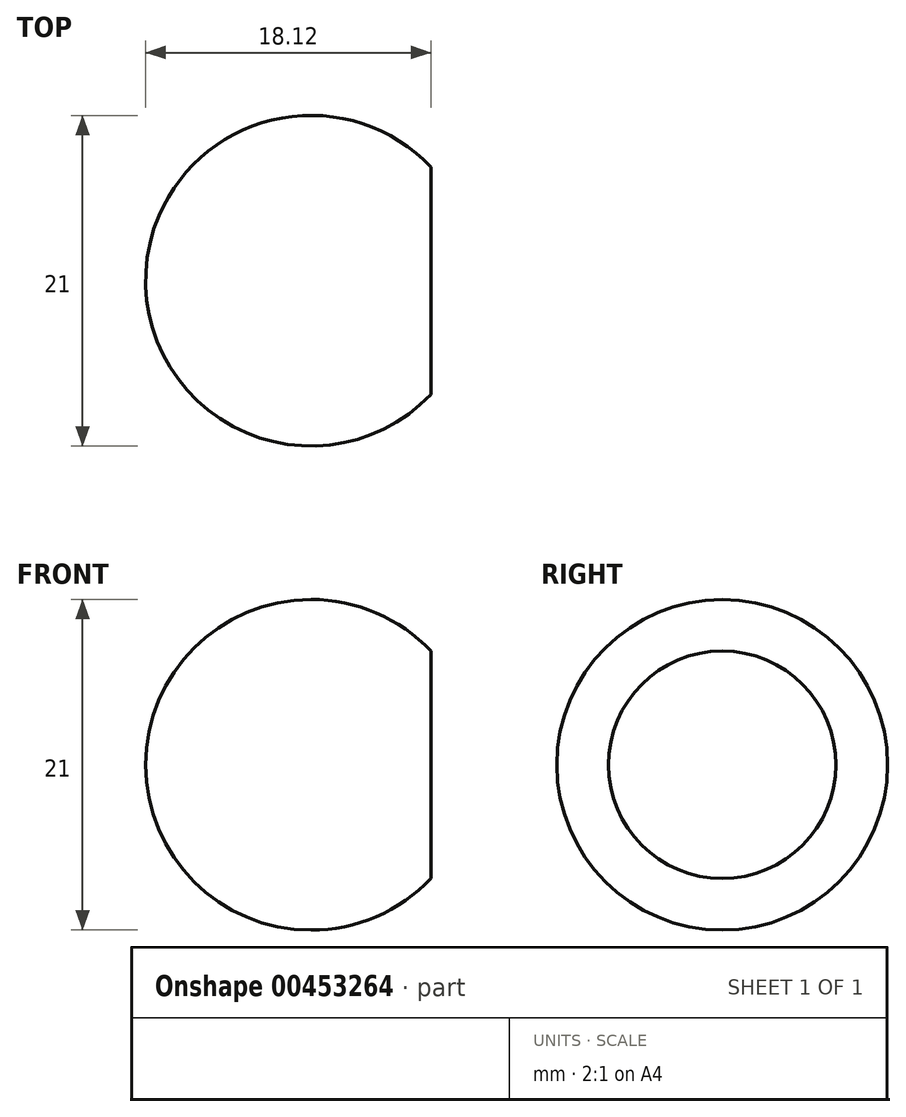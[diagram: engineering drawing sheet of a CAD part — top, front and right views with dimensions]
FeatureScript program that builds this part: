
annotation { "Feature Type Name" : "Feature", "Feature Type Description" : "" }
export const myFeature = defineFeature(function(context is Context, id is Id, definition is map)
    precondition{}
    {
        {
            var Q0;
            Q0=qCreatedBy(makeId("Right.planeOp"),FACE);
            var sketch = newSketch(context, id + "F0", { "sketchPlane" : qUnion([Q0])});
            skCircle(sketch, "E0", {"center": v(0, 0) * mm, "radius": 10.5 * mm});
            skLineSegment(sketch, "E1", {"start": v(0, 10.5) * mm, "end": v(0, -10.5) * mm});
            skSolve(sketch);
        }
        {
            var Q0;
            {var subQ0=sQuery(id+"F0.wireOp",EDGE,"E1");Q0=makeQuery(id+"F0.imprint","IMPRINT",FACE,{"disambiguationData":[TD([[makeQuery(id+"F0.imprint","IMPRINT",EDGE,{"derivedFrom":subQ0}),1.0]])]});}
            var Q1;
            Q1=sQuery(id+"F0.wireOp",EDGE,"E1");
            revolve(context, id + "F1", {"entities" : qUnion([Q0]), "axis" : qUnion([Q1]), "revolveType" : RevolveType.FULL});
        }
        {
            var Q0;
            Q0=qCreatedBy(makeId("Right.planeOp"),FACE);
            cPlane(context, id + "F2", {"entities" : qUnion([Q0]), "cplaneType" : CPlaneType.OFFSET, "offset" : 7.62 * mm, "width" : 152.4 * mm, "height" : 152.4 * mm});
        }
        {
            var Q0;
            Q0=qCreatedBy(id+"F2.planeOp",FACE);
            var sketch = newSketch(context, id + "F3", { "sketchPlane" : qUnion([Q0])});
            skCircle(sketch, "E2", {"center": v(0, 0) * mm, "radius": 8.04 * mm});
            skSolve(sketch);
        }
        {
            var Q0;
            Q0=qSketchRegion(id+"F3",true);
            extrude(context, id + "F4", {"entities" : qUnion([Q0]), "operationType" : NewBodyOperationType.REMOVE, "depth" : 25.4 * mm});
        }
    });
